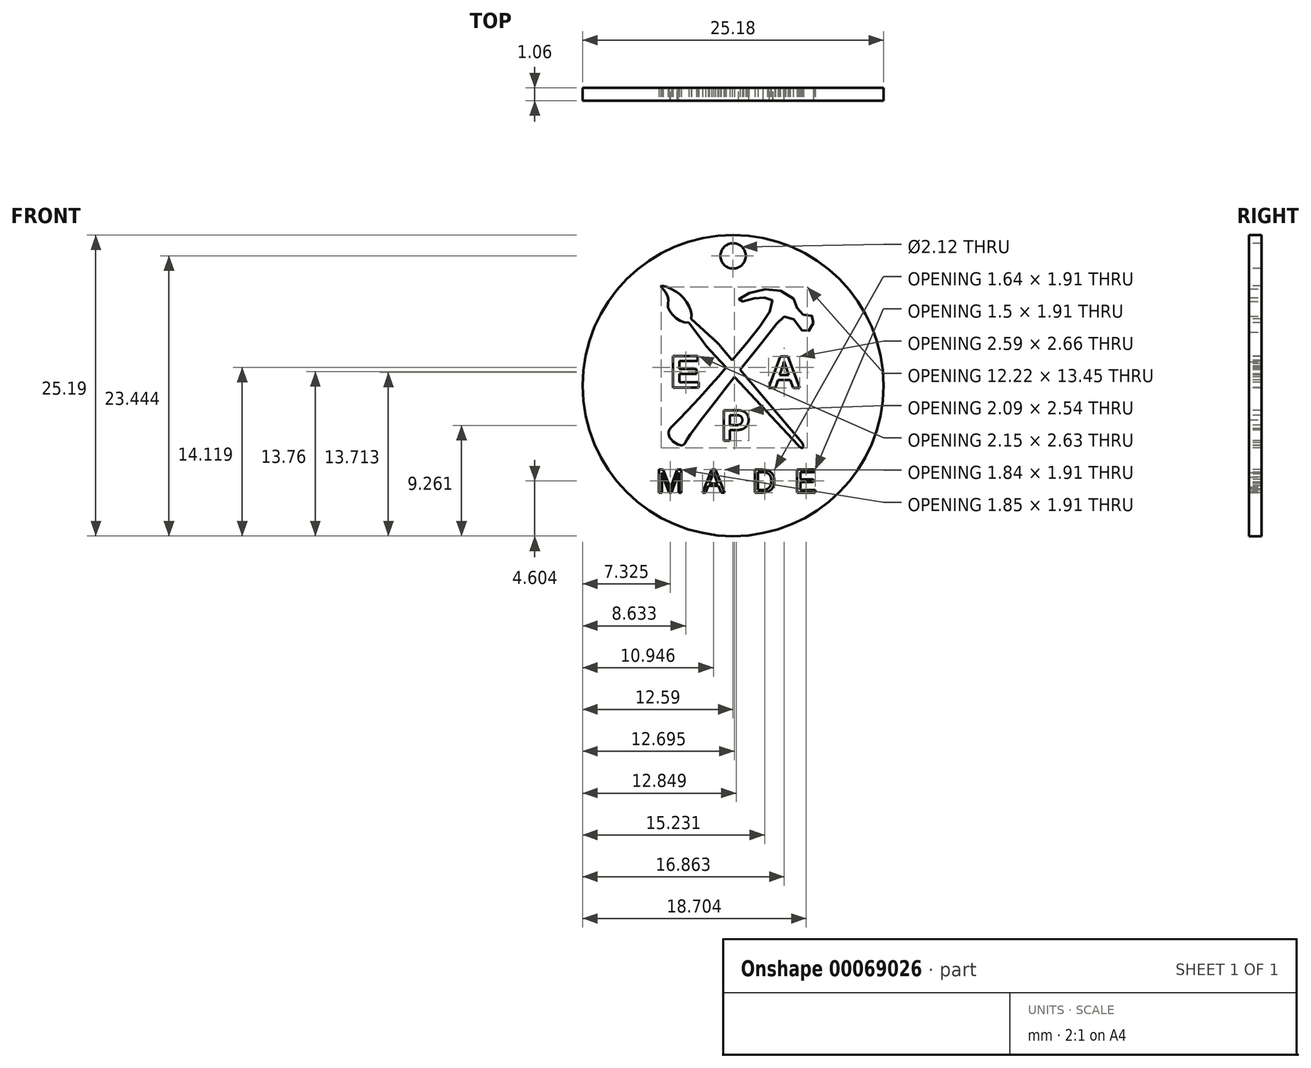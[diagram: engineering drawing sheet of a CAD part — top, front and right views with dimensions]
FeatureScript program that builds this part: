
annotation { "Feature Type Name" : "Feature", "Feature Type Description" : "" }
export const myFeature = defineFeature(function(context is Context, id is Id, definition is map)
    precondition{}
    {
        {
            var Q0;
            Q0=qCreatedBy(makeId("Front.planeOp"),FACE);
            var sketch = newSketch(context, id + "F0", { "sketchPlane" : qUnion([Q0])});
            skCircle(sketch, "E0", {"center": v(0, -4.2) * mm, "radius": 37.78 * mm});
            skSolve(sketch);
        }
        {
            var Q0;
            Q0=qCreatedBy(makeId("Front.planeOp"),FACE);
            var sketch = newSketch(context, id + "F1", { "sketchPlane" : qUnion([Q0])});
            skFitSpline(sketch, "E1", {"points": [v(9.42, 14.8) * mm, v(4.6, 7.97) * mm, v(-4.24, -2.51) * mm, v(-14.73, -13.87) * mm, v(-16.07, -15.4) * mm, v(-15.88, -17.33) * mm, v(-12.94, -19.23) * mm, v(-11.72, -18) * mm, v(-4.55, -8.27) * mm, v(10.67, 11.05) * mm, v(12.79, 13.07) * mm, v(14.9, 12.69) * mm, v(17.5, 9.51) * mm, v(18.78, 9.4) * mm, v(19.75, 10.6) * mm, v(20.23, 12.51) * mm, v(19.61, 13.39) * mm, v(17.64, 13.62) * mm, v(16.13, 15) * mm, v(15.6, 16.98) * mm, v(11.5, 19.73) * mm, v(5.44, 19.47) * mm, v(1.53, 17.62) * mm, v(1.48, 17.15) * mm, v(2.29, 16.91) * mm, v(5.35, 17.7) * mm, v(7.9, 17.85) * mm, v(9.71, 17.47) * mm, v(9.42, 14.8) * mm]});
            skSolve(sketch);
        }
        {
            var Q0;
            Q0 = qSketchRegion(id + "F0", true);
            extrude(context, id + "F2", {"entities" : qUnion([Q0]), "oppositeDirection" : true, "depth" : 3.17 * mm});
        }
        {
            var Q0;
            Q0 = qSketchRegion(id + "F1", true);
            extrude(context, id + "F3", {"entities" : qUnion([Q0]), "operationType" : NewBodyOperationType.REMOVE, "endBound" : BoundingType.THROUGH_ALL, "oppositeDirection" : true, "depth" : 1.27 * mm});
        }
        {
            var Q0;
            Q0=qCreatedBy(makeId("Front.planeOp"),FACE);
            var sketch = newSketch(context, id + "F4", { "sketchPlane" : qUnion([Q0])});
            skLineSegment(sketch, "E2", {"start": v(-10.54, 12.6) * mm, "end": v(-5.08, 7.64) * mm});
            skLineSegment(sketch, "E3", {"start": v(-2.77, 5.24) * mm, "end": v(17.27, -18.47) * mm});
            skLineSegment(sketch, "E4", {"start": v(16.34, -19.18) * mm, "end": v(-5.67, 4.55) * mm});
            skLineSegment(sketch, "E5", {"start": v(-7.42, 6.64) * mm, "end": v(-11.09, 11.57) * mm});
            skPoint(sketch, "E6.visualSharp", {"position": v(-3.85, 6.52) * mm});
            skArc(sketch, "E6.filletArc", {"start": v(-2.77, 5.24) * mm, "mid": v(-3.89, 6.48) * mm, "end": v(-5.08, 7.64) * mm});
            skPoint(sketch, "E7.visualSharp", {"position": v(-6.6, 5.55) * mm});
            skArc(sketch, "E7.filletArc", {"start": v(-7.42, 6.64) * mm, "mid": v(-6.57, 5.57) * mm, "end": v(-5.67, 4.55) * mm});
            skFitSpline(sketch, "E8", {"points": [v(-10.54, 12.6) * mm, v(-10.54, 14.33) * mm, v(-11.4, 16.34) * mm, v(-13.32, 18.7) * mm, v(-15.33, 20) * mm, v(-17.66, 20.86) * mm, v(-18.11, 20.77) * mm, v(-17.84, 20.36) * mm, v(-16.45, 18.34) * mm, v(-16.31, 16.88) * mm, v(-16.27, 15.35) * mm, v(-15.2, 13.6) * mm, v(-13.2, 12.02) * mm, v(-11.09, 11.57) * mm], "startDerivative": vector(2.69, 23.7) * mm, "endDerivative": vector(25.97, -2.9) * mm});
            skFitSpline(sketch, "E9", {"points": [v(17.27, -18.47) * mm, v(17.6, -19.27) * mm, v(17.5, -19.78) * mm, v(16.76, -19.6) * mm, v(16.34, -19.18) * mm], "startDerivative": vector(1.32, -2.83) * mm, "endDerivative": vector(-1.34, 1.87) * mm});
            skSolve(sketch);
        }
        {
            var Q0;
            Q0 = qSketchRegion(id + "F4", true);
            extrude(context, id + "F5", {"entities" : qUnion([Q0]), "operationType" : NewBodyOperationType.REMOVE, "endBound" : BoundingType.THROUGH_ALL, "oppositeDirection" : true, "depth" : 1.27 * mm});
        }
        {
            var Q0;
            Q0=makeQuery(id+"F2.opExtrude","CAP_FACE",FACE,{"disambiguationData":[OSD([sQuery(id+"F0.wireOp",EDGE,"E0")])],"isStart":true});
            var sketch = newSketch(context, id + "F6", { "sketchPlane" : qUnion([Q0])});
            skText(sketch, "E10", { "text": "A", "fontName": "Arimo-Bold.ttf"});
            skText(sketch, "E11", { "text": "P", "fontName": "Arimo-Bold.ttf"});
            skText(sketch, "E12", { "text": "E", "fontName": "Arimo-Bold.ttf"});
            const initialGuessF6  = {"E10": [0.00864, -0.00482, 1, 0, 0.00835], "E11": [-0.0031, -0.018, 1, 0, 0.00798], "E12": [-0.01586, -0.00464, 1, 0, 0.00827]};
            skSetInitialGuess(sketch, initialGuessF6);
            skSolve(sketch);
        }
        {
            var Q0;
            Q0 = qSketchRegion(id + "F6", true);
            extrude(context, id + "F7", {"entities" : qUnion([Q0]), "operationType" : NewBodyOperationType.REMOVE, "endBound" : BoundingType.THROUGH_ALL, "oppositeDirection" : true, "depth" : 1.27 * mm});
        }
        {
            var Q0;
            {var subQ1=sQuery(id+"F0.wireOp",EDGE,"E0");Q0=makeQuery(id+"F7.boolean.opBoolean","SPLIT",FACE,{"disambiguationData":[TD([makeQuery(id+"F2.opExtrude","SWEPT_FACE",FACE,{"disambiguationData":[OSD([subQ1])]})])],"derivedFrom":makeQuery(id+"F2.opExtrude","CAP_FACE",FACE,{"disambiguationData":[OSD([subQ1])],"isStart":true})});}
            var sketch = newSketch(context, id + "F8", { "sketchPlane" : qUnion([Q0])});
            skText(sketch, "E13", { "text": "M  A   D  E", "fontName": "Arimo-Regular.ttf"});
            const initialGuessF8  = {"E13": [-0.01926, -0.03102, 1, 0, 0.00599]};
            skSetInitialGuess(sketch, initialGuessF8);
            skSolve(sketch);
        }
        {
            var Q0;
            Q0 = qSketchRegion(id + "F8", true);
            extrude(context, id + "F9", {"entities" : qUnion([Q0]), "operationType" : NewBodyOperationType.REMOVE, "endBound" : BoundingType.THROUGH_ALL, "oppositeDirection" : true, "depth" : 1.27 * mm});
        }
        {
            var Q0;
            {var subQ31=sQuery(id+"F0.wireOp",EDGE,"E0");var subQ32=makeQuery(id+"F2.opExtrude","SWEPT_FACE",FACE,{"disambiguationData":[OSD([subQ31])]});Q0=makeQuery(id+"F9.boolean.opBoolean","SPLIT",FACE,{"disambiguationData":[TD([subQ32])],"derivedFrom":makeQuery(id+"F7.boolean.opBoolean","SPLIT",FACE,{"disambiguationData":[TD([subQ32])],"derivedFrom":makeQuery(id+"F2.opExtrude","CAP_FACE",FACE,{"disambiguationData":[OSD([subQ31])],"isStart":true})})});}
            var sketch = newSketch(context, id + "F10", { "sketchPlane" : qUnion([Q0])});
            skCircle(sketch, "E14", {"center": v(0, 28.36) * mm, "radius": 3.17 * mm});
            skSolve(sketch);
        }
        {
            var Q0;
            Q0 = qSketchRegion(id + "F10", true);
            extrude(context, id + "F11", {"entities" : qUnion([Q0]), "operationType" : NewBodyOperationType.REMOVE, "endBound" : BoundingType.THROUGH_ALL, "oppositeDirection" : true, "depth" : 25.4 * mm});
        }
        {
            var Q0;
            Q0=makeQuery(id+"F7.boolean.opBoolean","SPLIT",BODY,{"disambiguationData":[OD(1.0)],"derivedFrom":makeQuery(id+"F2.opExtrude","SWEPT_BODY",BODY,{"disambiguationData":[OSD([sQuery(id+"F0.wireOp",EDGE,"E0")])]})});
            var Q1;
            Q1=makeQuery(id+"F7.boolean.opBoolean","SPLIT",BODY,{"disambiguationData":[OD(2.0)],"derivedFrom":makeQuery(id+"F2.opExtrude","SWEPT_BODY",BODY,{"disambiguationData":[OSD([sQuery(id+"F0.wireOp",EDGE,"E0")])]})});
            var Q2;
            Q2=makeQuery(id+"F9.boolean.opBoolean","SPLIT",BODY,{"disambiguationData":[OD(0.0)],"derivedFrom":makeQuery(id+"F7.boolean.opBoolean","SPLIT",BODY,{"disambiguationData":[OD(0.0)],"derivedFrom":makeQuery(id+"F2.opExtrude","SWEPT_BODY",BODY,{"disambiguationData":[OSD([sQuery(id+"F0.wireOp",EDGE,"E0")])]})})});
            var Q3;
            Q3=makeQuery(id+"F9.boolean.opBoolean","SPLIT",BODY,{"disambiguationData":[OD(1.0)],"derivedFrom":makeQuery(id+"F7.boolean.opBoolean","SPLIT",BODY,{"disambiguationData":[OD(0.0)],"derivedFrom":makeQuery(id+"F2.opExtrude","SWEPT_BODY",BODY,{"disambiguationData":[OSD([sQuery(id+"F0.wireOp",EDGE,"E0")])]})})});
            var Q4;
            Q4=makeQuery(id+"F9.boolean.opBoolean","SPLIT",BODY,{"disambiguationData":[OD(2.0)],"derivedFrom":makeQuery(id+"F7.boolean.opBoolean","SPLIT",BODY,{"disambiguationData":[OD(0.0)],"derivedFrom":makeQuery(id+"F2.opExtrude","SWEPT_BODY",BODY,{"disambiguationData":[OSD([sQuery(id+"F0.wireOp",EDGE,"E0")])]})})});
            var Q5;
            Q5=qCreatedBy(makeId("Origin.pointOp"),VERTEX);
            transform(context, id + "F12", {"entities" : qUnion([Q0, Q1, Q2, Q3, Q4]), "transformType" : TransformType.SCALE_UNIFORMLY, "scale" : 1 / 3, "scalePoint" : qUnion([Q5]), "makeCopy" : false});
        }
    });
